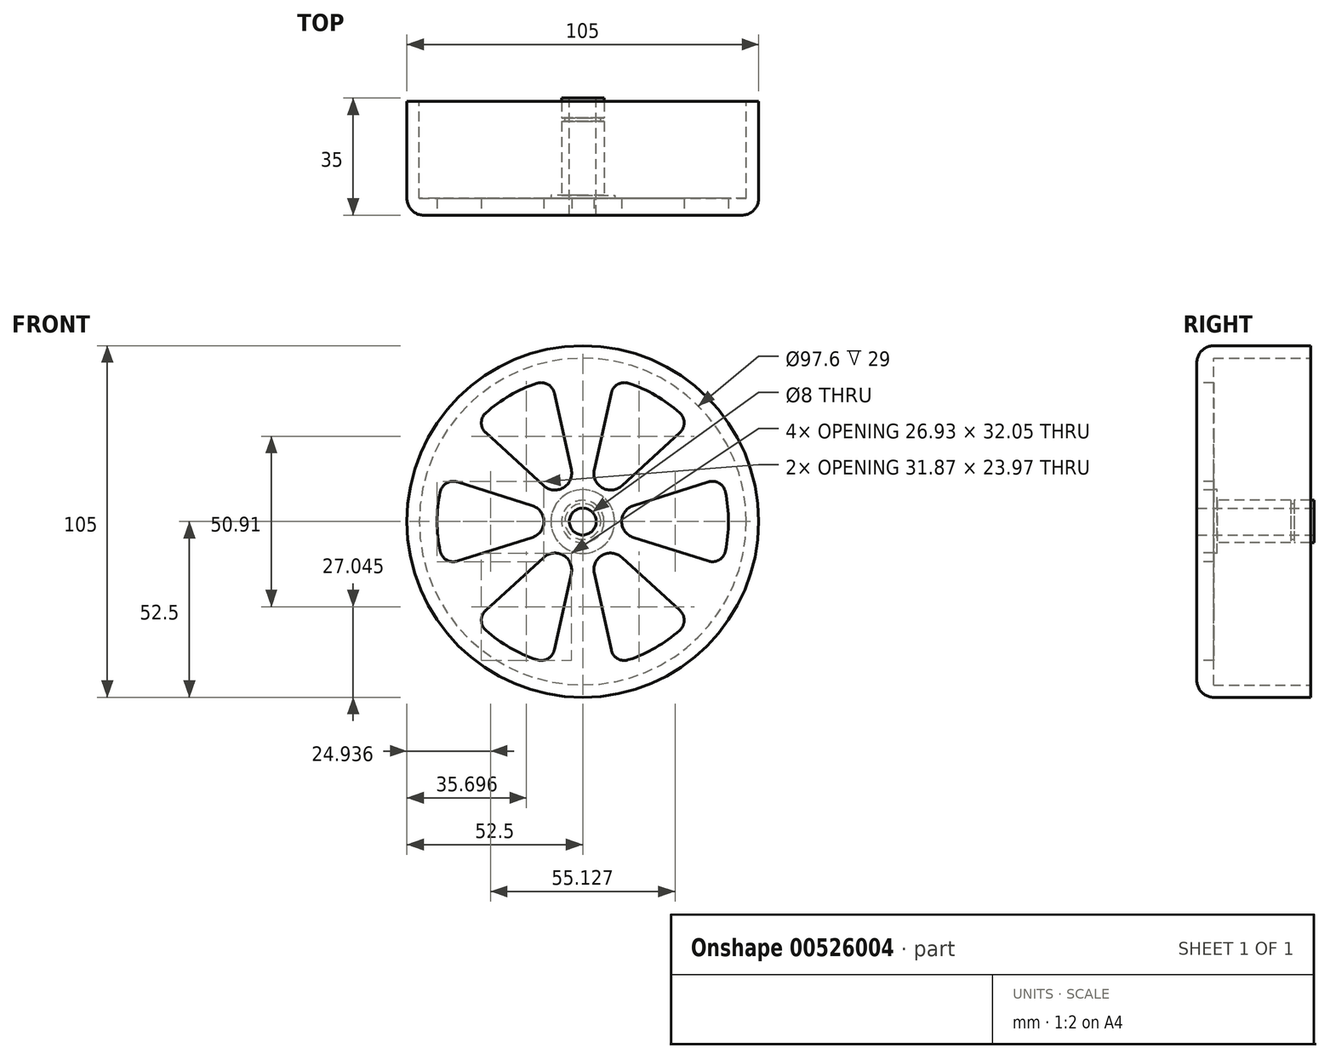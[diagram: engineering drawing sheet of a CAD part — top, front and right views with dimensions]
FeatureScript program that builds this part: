
annotation { "Feature Type Name" : "Feature", "Feature Type Description" : "" }
export const myFeature = defineFeature(function(context is Context, id is Id, definition is map)
    precondition{}
    {
        {
            var Q0;
            Q0=qCreatedBy(makeId("Front.planeOp"),FACE);
            var sketch = newSketch(context, id + "F0", { "sketchPlane" : qUnion([Q0])});
            skCircle(sketch, "E0", {"center": v(0, 0) * mm, "radius": 48.8 * mm});
            skCircle(sketch, "E1", {"center": v(0, 0) * mm, "radius": 52.5 * mm});
            skSolve(sketch);
        }
        {
            var Q0;
            Q0=qSketchRegion(id+"F0",true);
            extrude(context, id + "F1", {"entities" : qUnion([Q0]), "depth" : 29 * mm});
        }
        {
            var Q0;
            Q0=makeQuery(id+"F1.opExtrude","CAP_FACE",FACE,{"disambiguationData":[OSD([sQuery(id+"F0.wireOp",EDGE,"E0"),sQuery(id+"F0.wireOp",EDGE,"E1")])],"isStart":false});
            var sketch = newSketch(context, id + "F2", { "sketchPlane" : qUnion([Q0])});
            skCircle(sketch, "E2.0", {"center": v(0, 0) * mm, "radius": 52.5 * mm});
            skCircle(sketch, "E3", {"center": v(0, 0) * mm, "radius": 4 * mm});
            skSolve(sketch);
        }
        {
            var Q0;
            Q0=qSketchRegion(id+"F2",true);
            extrude(context, id + "F3", {"entities" : qUnion([Q0]), "operationType" : NewBodyOperationType.ADD, "depth" : 5 * mm});
        }
        {
            var Q0;
            Q0=makeQuery(id+"F3.opExtrude","CAP_FACE",FACE,{"disambiguationData":[OSD([sQuery(id+"F2.wireOp",EDGE,"E2.0"),sQuery(id+"F2.wireOp",EDGE,"E3")])],"isStart":true});
            var sketch = newSketch(context, id + "F4", { "sketchPlane" : qUnion([Q0])});
            skCircle(sketch, "E4", {"center": v(0, 0) * mm, "radius": 6.35 * mm});
            skCircle(sketch, "E5.0", {"center": v(0, 0) * mm, "radius": 4 * mm});
            skSolve(sketch);
        }
        {
            var Q0;
            Q0=qSketchRegion(id+"F4",true);
            extrude(context, id + "F5", {"entities" : qUnion([Q0]), "operationType" : NewBodyOperationType.ADD, "depth" : 30 * mm});
        }
        {
            var Q0;
            Q0=makeQuery(id+"F5.opExtrude","CAP_FACE",FACE,{"disambiguationData":[OSD([sQuery(id+"F4.wireOp",EDGE,"E4"),sQuery(id+"F4.wireOp",EDGE,"E5.0")])],"isStart":false});
            cPlane(context, id + "F6", {"entities" : qUnion([Q0]), "cplaneType" : CPlaneType.OFFSET, "offset" : 6 * mm, "oppositeDirection" : true, "width" : 150 * mm, "height" : 150 * mm});
        }
        {
            var Q0;
            Q0=qCreatedBy(id+"F6.planeOp",FACE);
            var sketch = newSketch(context, id + "F7", { "sketchPlane" : qUnion([Q0])});
            skCircle(sketch, "E6", {"center": v(0, 0) * mm, "radius": 6.85 * mm});
            skCircle(sketch, "E7", {"center": v(0, 0) * mm, "radius": 5.35 * mm});
            skSolve(sketch);
        }
        {
            var Q0;
            Q0=qSketchRegion(id+"F7",true);
            extrude(context, id + "F8", {"entities" : qUnion([Q0]), "operationType" : NewBodyOperationType.REMOVE, "oppositeDirection" : true, "depth" : 1 * mm});
        }
        {
            var Q0;
            Q0=makeQuery(id+"F3.opExtrude","CAP_FACE",FACE,{"disambiguationData":[OSD([sQuery(id+"F2.wireOp",EDGE,"E2.0"),sQuery(id+"F2.wireOp",EDGE,"E3")])],"isStart":true});
            var sketch = newSketch(context, id + "F9", { "sketchPlane" : qUnion([Q0])});
            skCircle(sketch, "E8", {"center": v(0, 0) * mm, "radius": 9.53 * mm});
            skCircle(sketch, "E9", {"center": v(0, 0) * mm, "radius": 4.38 * mm});
            skSolve(sketch);
        }
        {
            var Q0;
            Q0=qSketchRegion(id+"F9",true);
            extrude(context, id + "F10", {"entities" : qUnion([Q0]), "operationType" : NewBodyOperationType.ADD, "depth" : 1 * mm});
        }
        {
            var Q0;
            Q0=makeQuery(id+"F3.opExtrude","CAP_EDGE",EDGE,{"disambiguationData":[OSD([sQuery(id+"F2.wireOp",EDGE,"E2.0")])],"isStart":false});
            fillet(context, id + "F11", {"entities" : qUnion([Q0]), "radius" : 5 * mm, "tangentPropagation" : true, "allowEdgeOverflow" : false});
        }
        {
            var Q0;
            Q0=makeQuery(id+"F3.opExtrude","CAP_FACE",FACE,{"disambiguationData":[OSD([sQuery(id+"F2.wireOp",EDGE,"E2.0"),sQuery(id+"F2.wireOp",EDGE,"E3")])],"isStart":false});
            var sketch = newSketch(context, id + "F12", { "sketchPlane" : qUnion([Q0])});
            skArc(sketch, "E10", {"start": v(42.6, 8.81) * mm, "mid": v(43.5, 0) * mm, "end": v(42.6, -8.81) * mm});
            skLineSegment(sketch, "E11", {"start": v(37.48, 11.82) * mm, "end": v(15.12, 4.77) * mm});
            skLineSegment(sketch, "E12", {"start": v(15.12, -4.77) * mm, "end": v(37.48, -11.82) * mm});
            skArc(sketch, "E13.filletArc", {"start": v(15.12, 4.77) * mm, "mid": v(11.63, 0) * mm, "end": v(15.12, -4.77) * mm});
            skPoint(sketch, "E14.visualSharp", {"position": v(41.49, 13.08) * mm});
            skArc(sketch, "E14.filletArc", {"start": v(42.6, 8.81) * mm, "mid": v(40.7, 11.45) * mm, "end": v(37.48, 11.82) * mm});
            skPoint(sketch, "E15.visualSharp", {"position": v(41.49, -13.08) * mm});
            skArc(sketch, "E15.filletArc", {"start": v(37.48, -11.82) * mm, "mid": v(40.7, -11.45) * mm, "end": v(42.6, -8.81) * mm});
            skArc(sketch, "E16.1.0", {"start": v(13.67, 41.3) * mm, "mid": v(21.75, 37.67) * mm, "end": v(28.93, 32.48) * mm});
            skLineSegment(sketch, "E16.1.1", {"start": v(11.7, 10.71) * mm, "end": v(28.97, 26.55) * mm});
            skPoint(sketch, "E16.1.2", {"position": v(9.42, 42.47) * mm});
            skArc(sketch, "E16.1.3", {"start": v(3.43, 15.48) * mm, "mid": v(5.81, 10.07) * mm, "end": v(11.7, 10.71) * mm});
            skLineSegment(sketch, "E16.1.4", {"start": v(8.5, 38.37) * mm, "end": v(3.43, 15.48) * mm});
            skArc(sketch, "E16.1.5", {"start": v(13.67, 41.3) * mm, "mid": v(10.44, 40.98) * mm, "end": v(8.5, 38.37) * mm});
            skArc(sketch, "E16.1.6", {"start": v(28.97, 26.55) * mm, "mid": v(30.27, 29.53) * mm, "end": v(28.93, 32.48) * mm});
            skPoint(sketch, "E16.1.7", {"position": v(32.07, 29.39) * mm});
            skArc(sketch, "E16.2.0", {"start": v(-28.93, 32.48) * mm, "mid": v(-21.75, 37.67) * mm, "end": v(-13.67, 41.3) * mm});
            skLineSegment(sketch, "E16.2.1", {"start": v(-3.43, 15.48) * mm, "end": v(-8.5, 38.37) * mm});
            skPoint(sketch, "E16.2.2", {"position": v(-32.07, 29.39) * mm});
            skArc(sketch, "E16.2.3", {"start": v(-11.7, 10.71) * mm, "mid": v(-5.81, 10.07) * mm, "end": v(-3.43, 15.48) * mm});
            skLineSegment(sketch, "E16.2.4", {"start": v(-28.97, 26.55) * mm, "end": v(-11.7, 10.71) * mm});
            skArc(sketch, "E16.2.5", {"start": v(-28.93, 32.48) * mm, "mid": v(-30.27, 29.53) * mm, "end": v(-28.97, 26.55) * mm});
            skArc(sketch, "E16.2.6", {"start": v(-8.5, 38.37) * mm, "mid": v(-10.44, 40.98) * mm, "end": v(-13.67, 41.3) * mm});
            skPoint(sketch, "E16.2.7", {"position": v(-9.42, 42.47) * mm});
            skArc(sketch, "E16.3.0", {"start": v(-42.6, -8.81) * mm, "mid": v(-43.5, 0) * mm, "end": v(-42.6, 8.81) * mm});
            skLineSegment(sketch, "E16.3.1", {"start": v(-15.12, 4.77) * mm, "end": v(-37.48, 11.82) * mm});
            skPoint(sketch, "E16.3.2", {"position": v(-41.49, -13.08) * mm});
            skArc(sketch, "E16.3.3", {"start": v(-15.12, -4.77) * mm, "mid": v(-11.63, 0) * mm, "end": v(-15.12, 4.77) * mm});
            skLineSegment(sketch, "E16.3.4", {"start": v(-37.48, -11.82) * mm, "end": v(-15.12, -4.77) * mm});
            skArc(sketch, "E16.3.5", {"start": v(-42.6, -8.81) * mm, "mid": v(-40.7, -11.45) * mm, "end": v(-37.48, -11.82) * mm});
            skArc(sketch, "E16.3.6", {"start": v(-37.48, 11.82) * mm, "mid": v(-40.7, 11.45) * mm, "end": v(-42.6, 8.81) * mm});
            skPoint(sketch, "E16.3.7", {"position": v(-41.49, 13.08) * mm});
            skArc(sketch, "E16.4.0", {"start": v(-13.67, -41.3) * mm, "mid": v(-21.75, -37.67) * mm, "end": v(-28.93, -32.48) * mm});
            skLineSegment(sketch, "E16.4.1", {"start": v(-11.7, -10.71) * mm, "end": v(-28.97, -26.55) * mm});
            skPoint(sketch, "E16.4.2", {"position": v(-9.42, -42.47) * mm});
            skArc(sketch, "E16.4.3", {"start": v(-3.43, -15.48) * mm, "mid": v(-5.81, -10.07) * mm, "end": v(-11.7, -10.71) * mm});
            skLineSegment(sketch, "E16.4.4", {"start": v(-8.5, -38.37) * mm, "end": v(-3.43, -15.48) * mm});
            skArc(sketch, "E16.4.5", {"start": v(-13.67, -41.3) * mm, "mid": v(-10.44, -40.98) * mm, "end": v(-8.5, -38.37) * mm});
            skArc(sketch, "E16.4.6", {"start": v(-28.97, -26.55) * mm, "mid": v(-30.27, -29.53) * mm, "end": v(-28.93, -32.48) * mm});
            skPoint(sketch, "E16.4.7", {"position": v(-32.07, -29.39) * mm});
            skArc(sketch, "E16.5.0", {"start": v(28.93, -32.48) * mm, "mid": v(21.75, -37.67) * mm, "end": v(13.67, -41.3) * mm});
            skLineSegment(sketch, "E16.5.1", {"start": v(3.43, -15.48) * mm, "end": v(8.5, -38.37) * mm});
            skPoint(sketch, "E16.5.2", {"position": v(32.07, -29.39) * mm});
            skArc(sketch, "E16.5.3", {"start": v(11.7, -10.71) * mm, "mid": v(5.81, -10.07) * mm, "end": v(3.43, -15.48) * mm});
            skLineSegment(sketch, "E16.5.4", {"start": v(28.97, -26.55) * mm, "end": v(11.7, -10.71) * mm});
            skArc(sketch, "E16.5.5", {"start": v(28.93, -32.48) * mm, "mid": v(30.27, -29.53) * mm, "end": v(28.97, -26.55) * mm});
            skArc(sketch, "E16.5.6", {"start": v(8.5, -38.37) * mm, "mid": v(10.44, -40.98) * mm, "end": v(13.67, -41.3) * mm});
            skPoint(sketch, "E16.5.7", {"position": v(9.42, -42.47) * mm});
            skSolve(sketch);
        }
        {
            var Q0;
            Q0=qSketchRegion(id+"F12",true);
            extrude(context, id + "F13", {"entities" : qUnion([Q0]), "operationType" : NewBodyOperationType.REMOVE, "oppositeDirection" : true, "depth" : 25 * mm});
        }
    });
